# Revit family: Spot 3.4
name_source: partatom
category: Lighting Fixtures
revit_build: Autodesk Revit 2017 (Build: 20170419_0315(x64)
units: mm (PartAtom-declared; Revit-internal decimal feet)

## family parameters
Always vertical = No
Cut with Voids When Loaded = No
Light Source = No
OmniClass Number = 23.80.70.00
OmniClass Title = Lighting
Part Type = Normal
Room Calculation Point = Yes
Round Connector Dimension = Use Diameter
Shared = No
Work Plane-Based = No

## types (3) — shared parameters
Apparent Load Phase 1 = 15 W
Base = L&L_Stainless steel
Base bracket = Spot3.4_Base braket
Body = L&L_White
Bracket = L&L_Grey aluminium
CRI = 80
Code = CF3410000050SH Anthracite; CF3410000050SE White
Control system = -
Cutout dimensions = -
Delivered lumen output = 1042 lm (3000K, 39°)
Description = Outdoor projectors
Energy efficiency class = A A+ A++
Features = -
Geometry = Spot3.4_mod
Height mm = 181 mm  [stored 0.593832 ft]
IP = 66
LED Colour = 3000K (also available: 4000K - ref. URL Technical sheet)
Length mm = 120 mm  [stored 0.393701 ft]
Lens = L&L_Tempered extra-clear glass
Lumen output at source = 1476 lm (3000K)
Manufacturer = L&L Luce&Light
Material = body in anticorodal aluminium, screen in serigraphed, transparent and tempered extra-clear glass
Model = Spot 3.4
Mounting = surface mounted (ceiling, wall, ground, spike)
No. and type of led = 1 COB LED, 3-step MacAdam, 50 000h L90 B10 (Ta 25°C)
Notes = -
Power = 15W
Power cables = includes 1,5 m neoprene cable H05RN-F 3x1,0 Ø7 mm
Power supply = 230Vac
Power supply unit = built-in
URL = https://www.lucelight.it
URL Accessories and power supply units = https://www.lucelight.it
URL Catalogue = https://www.lucelight.it
URL DXF = https://www.lucelight.it
URL Description = https://www.lucelight.it
URL General code = https://www.lucelight.it
URL IES Photometric file = https://www.lucelight.it
URL Image = https://www.lucelight.it
URL Technical sheet = https://www.lucelight.it
Vertical rotation max = 230.00°
Voltage = 230 V
Weight kg = 1.20 kg
Width mm = 84 mm  [stored 0.275591 ft]
Wiring = -

## per-type parameters (varying)
| type | Light Source | Optics |
| Spot 3.4_L 55° (15W 3000K 230Vac) | Light Source : L55° | 55° |
| Spot 3.4_M 39° (15W 3000K 230Vac) | Light Source : M39° | 39° |
| Spot 3.4_S 15° (15W 3000K 230Vac) | Light Source : S15° | 15° |

note: [stored X ft] marks values corroborated as IEEE doubles in the binary element streams (Revit-internal decimal feet)

## geometry (parser evidence)
native form markers: Blend x2, Sweep x11
no freeform markers — native parametric forms only
